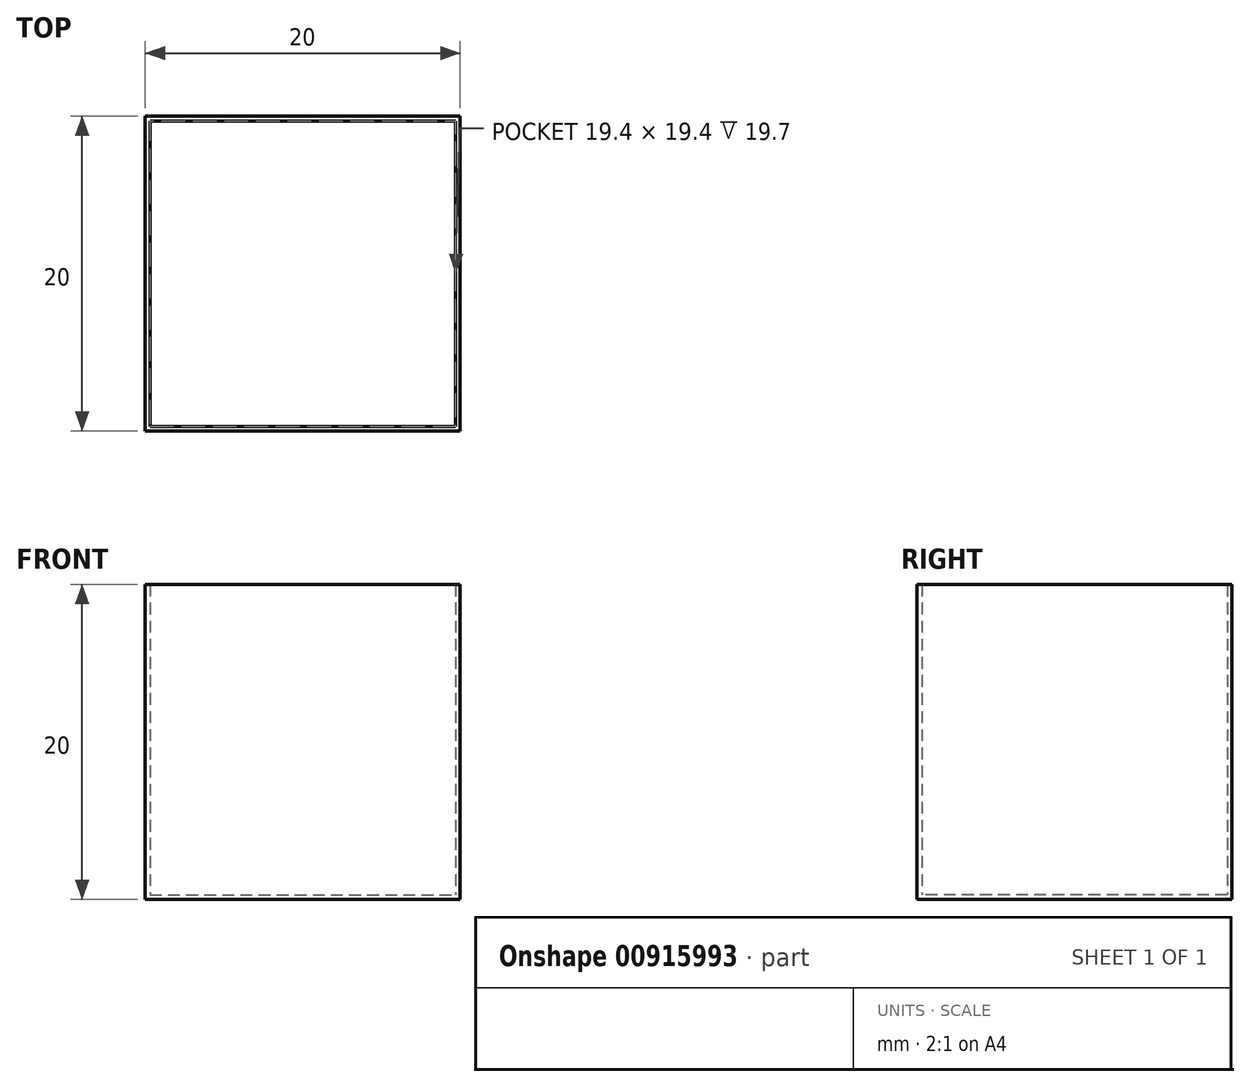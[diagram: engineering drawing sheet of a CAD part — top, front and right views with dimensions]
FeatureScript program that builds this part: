
annotation { "Feature Type Name" : "Feature", "Feature Type Description" : "" }
export const myFeature = defineFeature(function(context is Context, id is Id, definition is map)
    precondition{}
    {
        {
            assignVariable(context, id + "F0", {"name" : "t", "anyValue" : 0.3});
        }
        {
            assignVariable(context, id + "F1", {"name" : "l", "anyValue" : 20});
        }
        {
            var Q0;
            Q0=qCreatedBy(makeId("Top.planeOp"),FACE);
            var sketch = newSketch(context, id + "F2", { "sketchPlane" : qUnion([Q0])});
            skLineSegment(sketch, "E0.bottom", {"start": v(-10, 10) * mm, "end": v(10, 10) * mm});
            skLineSegment(sketch, "E0.top", {"start": v(-10, -10) * mm, "end": v(10, -10) * mm});
            skLineSegment(sketch, "E0.left", {"start": v(-10, 10) * mm, "end": v(-10, -10) * mm});
            skLineSegment(sketch, "E0.right", {"start": v(10, 10) * mm, "end": v(10, -10) * mm});
            skPoint(sketch, "E0.middle", {"position": v(0, 0) * mm});
            skSolve(sketch);
        }
        {
            var Q0;
            Q0 = qSketchRegion(id + "F2", true);
            extrude(context, id + "F3", {"entities" : qUnion([Q0]), "depth" : getVariable(context, 'l') * mm, "offsetDistance" : 25 * mm});
        }
        {
            var Q0;
            Q0=makeQuery(id+"F3.opExtrude","CAP_FACE",FACE,{"disambiguationData":[OSD([sQuery(id+"F2.wireOp",EDGE,"E0.bottom"),sQuery(id+"F2.wireOp",EDGE,"E0.top"),sQuery(id+"F2.wireOp",EDGE,"E0.left"),sQuery(id+"F2.wireOp",EDGE,"E0.right")])],"isStart":false});
            shell(context, id + "F4", {"entities" : qUnion([Q0]), "thickness" : (getVariable(context, 't')) * mm});
        }
    });
